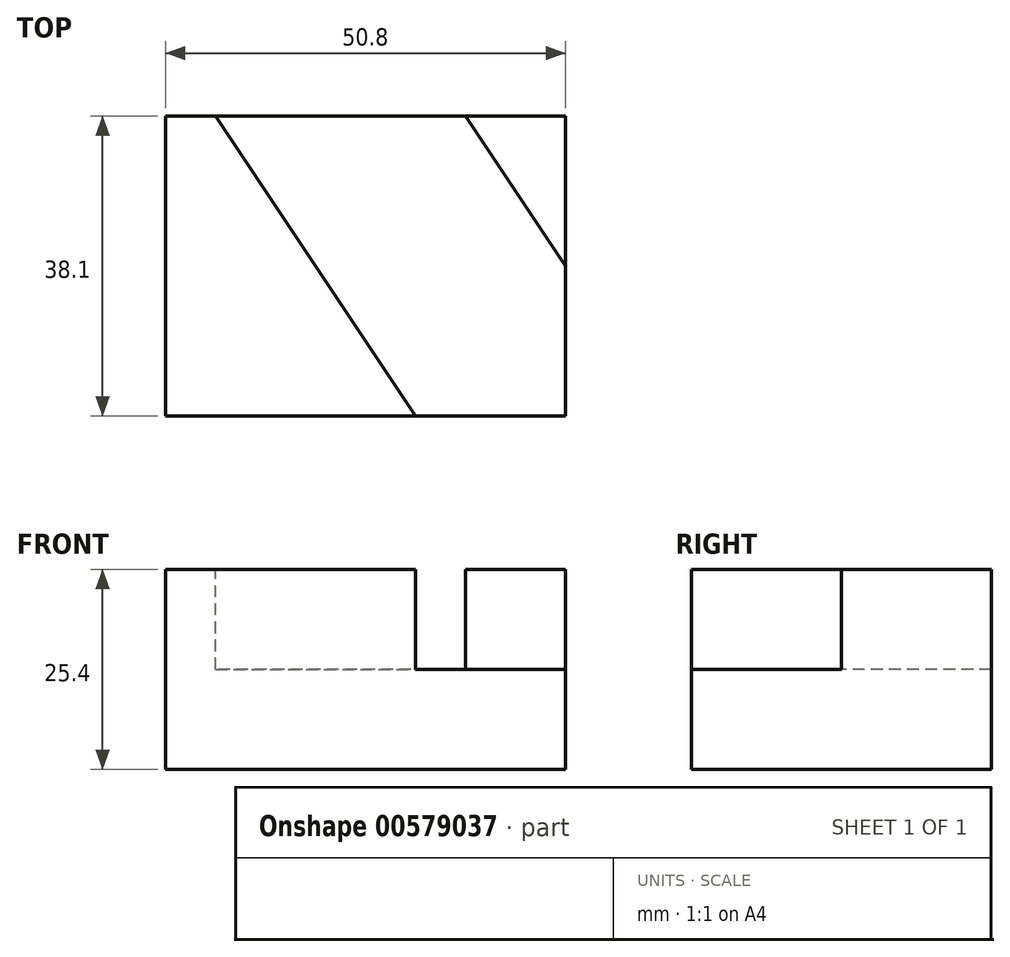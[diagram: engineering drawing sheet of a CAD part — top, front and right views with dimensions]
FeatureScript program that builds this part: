
annotation { "Feature Type Name" : "Feature", "Feature Type Description" : "" }
export const myFeature = defineFeature(function(context is Context, id is Id, definition is map)
    precondition{}
    {
        {
            var Q0;
            Q0=qCreatedBy(makeId("Front.planeOp"),FACE);
            var sketch = newSketch(context, id + "F0", { "sketchPlane" : qUnion([Q0])});
            skLineSegment(sketch, "E0", {"start": v(-84.49, 37.62) * mm, "end": v(-84.49, 12.22) * mm});
            skLineSegment(sketch, "E1", {"start": v(-84.49, 12.22) * mm, "end": v(-33.69, 12.22) * mm});
            skLineSegment(sketch, "E2", {"start": v(-33.69, 12.22) * mm, "end": v(-33.69, 37.62) * mm});
            skLineSegment(sketch, "E3", {"start": v(-33.69, 37.62) * mm, "end": v(-84.49, 37.62) * mm});
            skSolve(sketch);
        }
        {
            var Q0;
            Q0 = qSketchRegion(id + "F0", true);
            extrude(context, id + "F1", {"entities" : qUnion([Q0]), "depth" : 38.1 * mm, "offsetDistance" : 25.4 * mm});
        }
        {
            var Q0;
            Q0=makeQuery(id+"F1.opExtrude","SWEPT_FACE",FACE,{"disambiguationData":[OSD([sQuery(id+"F0.wireOp",EDGE,"E3")])]});
            var sketch = newSketch(context, id + "F2", { "sketchPlane" : qUnion([Q0])});
            skLineSegment(sketch, "E4", {"start": v(-78.14, 0) * mm, "end": v(-52.74, -38.1) * mm});
            skLineSegment(sketch, "E5", {"start": v(-52.74, -38.1) * mm, "end": v(-33.69, -38.1) * mm});
            skLineSegment(sketch, "E6", {"start": v(-33.69, -38.1) * mm, "end": v(-33.69, -19.05) * mm});
            skLineSegment(sketch, "E7", {"start": v(-33.69, -19.05) * mm, "end": v(-46.39, 0) * mm});
            skLineSegment(sketch, "E8", {"start": v(-46.39, 0) * mm, "end": v(-78.14, 0) * mm});
            skSolve(sketch);
        }
        {
            var Q0;
            Q0 = qSketchRegion(id + "F2", true);
            extrude(context, id + "F3", {"entities" : qUnion([Q0]), "operationType" : NewBodyOperationType.REMOVE, "oppositeDirection" : true, "depth" : 12.7 * mm, "offsetDistance" : 25.4 * mm});
        }
    });
